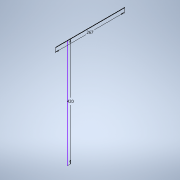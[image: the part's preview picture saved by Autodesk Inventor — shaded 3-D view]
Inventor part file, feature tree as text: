
AUTODESK INVENTOR PART (.ipt)
format: ipt  version: 2020 (Build 240168000, 168)  size: 85,504 bytes
history: native  units: in
note: dims shown in document units (in); Inventor stores cm internally (conversion verified against a paired STEP export)
features: sketch x1
ambient origin geometry x8: Origin, YZ Plane, XZ Plane, XY Plane, X Axis, Y Axis, Z Axis, Center Point
feature tree (1):
  sketch  "Sketch1"  dims[d0=10.5118in d1=16.5354in]
